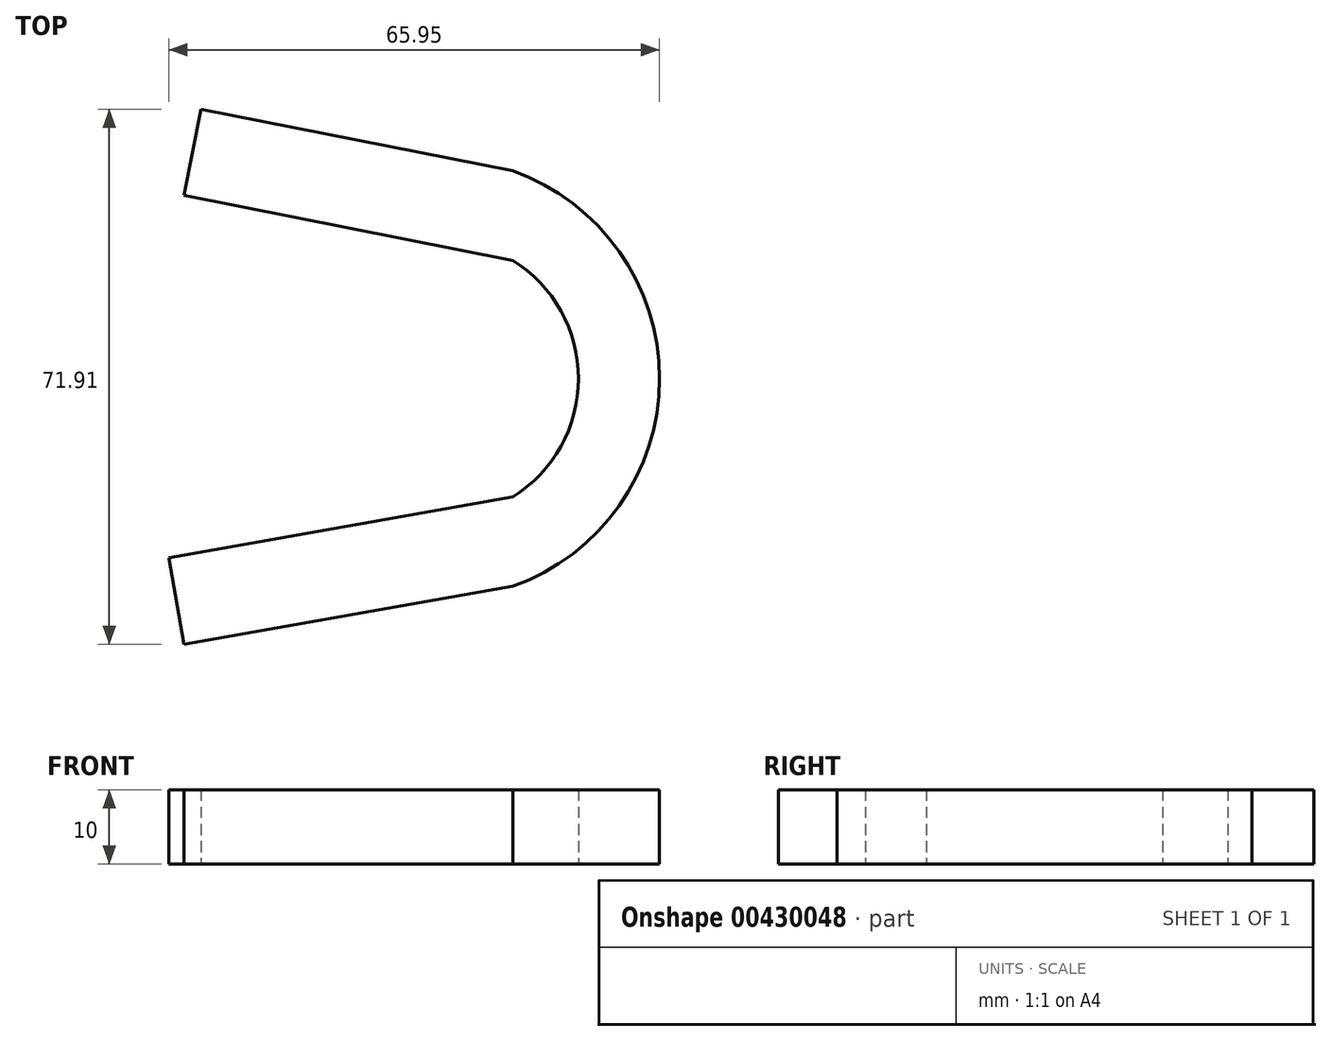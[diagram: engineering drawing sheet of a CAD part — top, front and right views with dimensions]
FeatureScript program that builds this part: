
annotation { "Feature Type Name" : "Feature", "Feature Type Description" : "" }
export const myFeature = defineFeature(function(context is Context, id is Id, definition is map)
    precondition{}
    {
        {
            var Q0;
            Q0=qCreatedBy(makeId("Top.planeOp"),FACE);
            var sketch = newSketch(context, id + "F0", { "sketchPlane" : qUnion([Q0])});
            skArc(sketch, "E0", {"start": v(9.87, -27.9) * mm, "mid": v(29.6, 0) * mm, "end": v(9.87, 27.9) * mm});
            skLineSegment(sketch, "E1", {"start": v(9.87, 27.9) * mm, "end": v(-32, 36.18) * mm});
            skLineSegment(sketch, "E2", {"start": v(-32, 36.18) * mm, "end": v(-34.29, 24.62) * mm});
            skLineSegment(sketch, "E3", {"start": v(-34.29, 24.62) * mm, "end": v(9.87, 15.9) * mm});
            skLineSegment(sketch, "E4", {"start": v(9.87, -27.9) * mm, "end": v(-34.29, -35.73) * mm});
            skLineSegment(sketch, "E5", {"start": v(-34.29, -35.73) * mm, "end": v(-36.35, -24.08) * mm});
            skLineSegment(sketch, "E6", {"start": v(-36.35, -24.08) * mm, "end": v(9.87, -15.9) * mm});
            skArc(sketch, "E7", {"start": v(9.87, -15.9) * mm, "mid": v(18.7, 0) * mm, "end": v(9.87, 15.9) * mm});
            skSolve(sketch);
        }
        {
            var Q0;
            Q0=makeQuery(id+"F0.imprint","IMPRINT",FACE,{"disambiguationData":[TD([[makeQuery(id+"F0.imprint","IMPRINT",EDGE,{"derivedFrom":sQuery(id+"F0.wireOp",EDGE,"E0")}),1.0]])]});
            extrude(context, id + "F1", {"entities" : qUnion([Q0]), "depth" : 10 * mm});
        }
    });
